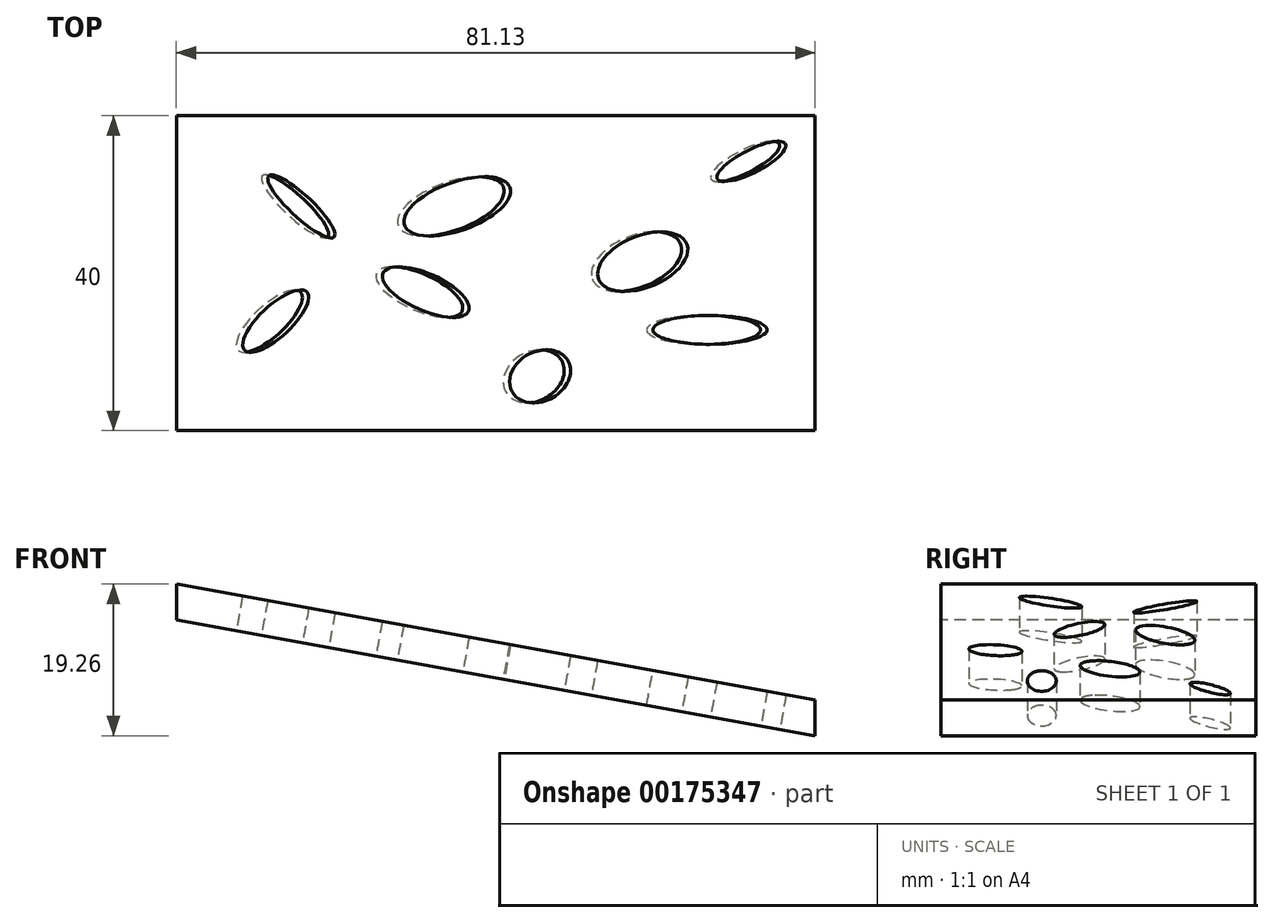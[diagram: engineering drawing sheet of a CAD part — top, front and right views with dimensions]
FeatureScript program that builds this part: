
annotation { "Feature Type Name" : "Feature", "Feature Type Description" : "" }
export const myFeature = defineFeature(function(context is Context, id is Id, definition is map)
    precondition{}
    {
        {
            var Q0;
            Q0=qCreatedBy(makeId("Front.planeOp"),FACE);
            var sketch = newSketch(context, id + "F0", { "sketchPlane" : qUnion([Q0])});
            skLineSegment(sketch, "E0", {"start": v(-50.25, 19.26) * mm, "end": v(30.88, 4.53) * mm});
            skLineSegment(sketch, "E1", {"start": v(30.88, 4.53) * mm, "end": v(30.88, 0) * mm});
            skLineSegment(sketch, "E2", {"start": v(30.88, 0) * mm, "end": v(-50.25, 14.72) * mm});
            skLineSegment(sketch, "E3", {"start": v(-50.25, 19.26) * mm, "end": v(-50.25, 14.72) * mm});
            skSolve(sketch);
        }
        {
            var Q0;
            Q0=makeQuery(id+"F0.imprint","IMPRINT",FACE,{"disambiguationData":[TD([[makeQuery(id+"F0.imprint","IMPRINT",EDGE,{"derivedFrom":sQuery(id+"F0.wireOp",EDGE,"E0")}),-1.0]])]});
            extrude(context, id + "F1", {"entities" : qUnion([Q0]), "oppositeDirection" : true, "depth" : 40 * mm});
        }
        {
            var Q0;
            Q0=makeQuery(id+"F1.opExtrude","SWEPT_FACE",FACE,{"disambiguationData":[OSD([sQuery(id+"F0.wireOp",EDGE,"E0")])]});
            var sketch = newSketch(context, id + "F2", { "sketchPlane" : qUnion([Q0])});
            skSolve(sketch);
        }
        {
            var Q0;
            {var subQ0=sQuery(id+"F0.wireOp",EDGE,"E0");Q0=makeQuery(id+"F2.imprint","IMPRINT",FACE,{"disambiguationData":[TD([[makeQuery(id+"F2.imprint","IMPRINT",EDGE,{"derivedFrom":makeQuery(id+"F1.opExtrude","CAP_EDGE",EDGE,{"disambiguationData":[OSD([subQ0])],"isStart":true})}),1.0]])]});}
            var sketch = newSketch(context, id + "F3", { "sketchPlane" : qUnion([Q0])});
            skEllipse(sketch, "E4", {"center": v(-36.74, 28.49) * mm, "majorRadius": 5.75 * mm, "minorRadius": 1.42 * mm, "majorAxis": v(0.74, -0.67)});
            skEllipse(sketch, "E5", {"center": v(-40.06, 13.91) * mm, "majorRadius": 5.49 * mm, "minorRadius": 2 * mm, "majorAxis": v(0.74, 0.67)});
            skEllipse(sketch, "E6", {"center": v(-20.7, 17.6) * mm, "majorRadius": 6.03 * mm, "minorRadius": 2.35 * mm, "majorAxis": v(0.92, -0.4)});
            skPoint(sketch, "E6.centerSnap0", {"position": v(-36, 17.6) * mm});
            skEllipse(sketch, "E7", {"center": v(-16.63, 28.49) * mm, "majorRadius": 7.24 * mm, "minorRadius": 3.09 * mm, "majorAxis": v(0.94, 0.33)});
            skEllipse(sketch, "E8", {"center": v(7.35, 21.48) * mm, "majorRadius": 6.13 * mm, "minorRadius": 3.31 * mm, "majorAxis": v(-0.93, -0.36)});
            skEllipse(sketch, "E9", {"center": v(16.02, 12.8) * mm, "majorRadius": 7.38 * mm, "minorRadius": 1.84 * mm, "majorAxis": v(-1, 0)});
            skEllipse(sketch, "E10", {"center": v(-5.93, 6.9) * mm, "majorRadius": 4.13 * mm, "minorRadius": 3.16 * mm, "majorAxis": v(0.9, 0.45)});
            skEllipse(sketch, "E11", {"center": v(21.37, 34.2) * mm, "majorRadius": 4.95 * mm, "minorRadius": 1.46 * mm, "majorAxis": v(-0.9, -0.45)});
            skSolve(sketch);
        }
        {
            var Q0;
            Q0 = qSketchRegion(id + "F3", true);
            extrude(context, id + "F4", {"entities" : qUnion([Q0]), "operationType" : NewBodyOperationType.REMOVE, "oppositeDirection" : true, "depth" : 25 * mm});
        }
    });
